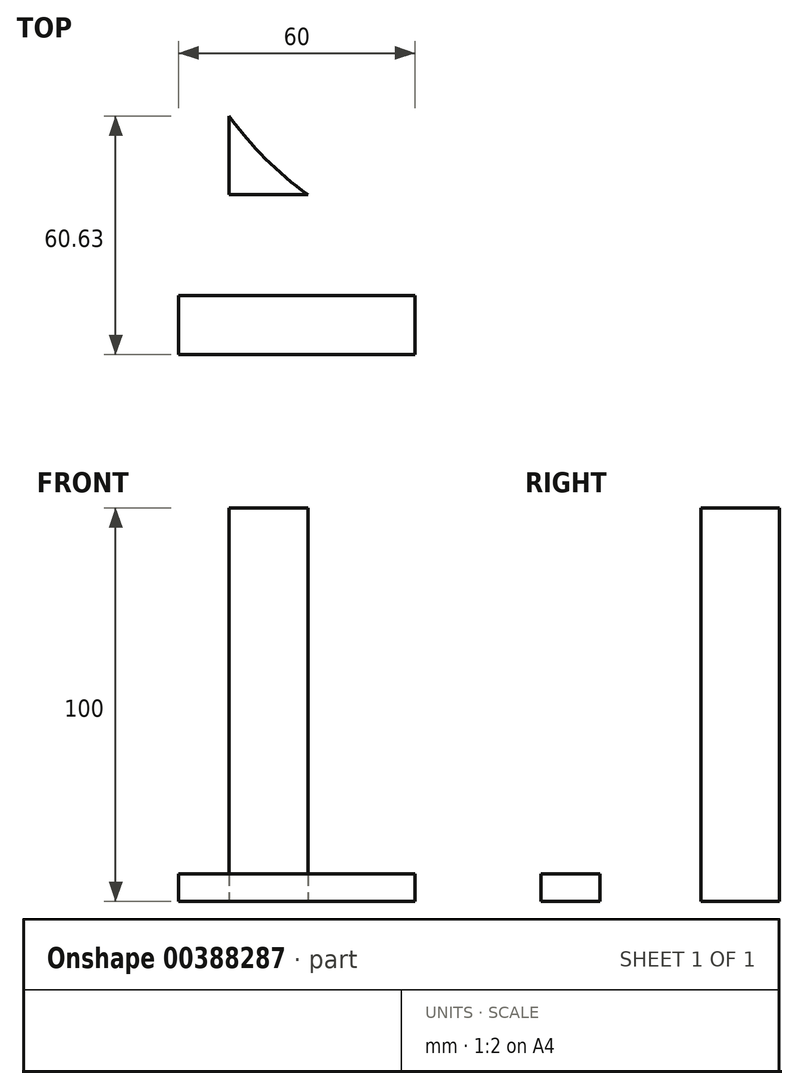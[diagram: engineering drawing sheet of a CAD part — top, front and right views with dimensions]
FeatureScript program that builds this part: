
annotation { "Feature Type Name" : "Feature", "Feature Type Description" : "" }
export const myFeature = defineFeature(function(context is Context, id is Id, definition is map)
    precondition{}
    {
        {
            var Q0;
            Q0=qCreatedBy(makeId("Top.planeOp"),FACE);
            var sketch = newSketch(context, id + "F0", { "sketchPlane" : qUnion([Q0])});
            skLineSegment(sketch, "E0.bottom", {"start": v(-10, -10) * mm, "end": v(10, -10) * mm});
            skLineSegment(sketch, "E0.left", {"start": v(-10, -10) * mm, "end": v(-10, 10) * mm});
            skArc(sketch, "E1", {"start": v(-10, 10) * mm, "mid": v(-0.8, -0.8) * mm, "end": v(10, -10) * mm});
            skSolve(sketch);
        }
        {
            var Q0;
            Q0 = qSketchRegion(id + "F0", true);
            extrude(context, id + "F1", {"entities" : qUnion([Q0]), "depth" : 100 * mm});
        }
        {
            var Q0;
            Q0=qCreatedBy(makeId("Top.planeOp"),FACE);
            var sketch = newSketch(context, id + "F2", { "sketchPlane" : qUnion([Q0])});
            skLineSegment(sketch, "E2.bottom", {"start": v(-22.8, -35.63) * mm, "end": v(37.2, -35.63) * mm});
            skLineSegment(sketch, "E2.top", {"start": v(-22.8, -50.63) * mm, "end": v(37.2, -50.63) * mm});
            skLineSegment(sketch, "E2.left", {"start": v(-22.8, -35.63) * mm, "end": v(-22.8, -50.63) * mm});
            skLineSegment(sketch, "E2.right", {"start": v(37.2, -35.63) * mm, "end": v(37.2, -50.63) * mm});
            skSolve(sketch);
        }
        {
            var Q0;
            Q0 = qSketchRegion(id + "F2", true);
            extrude(context, id + "F3", {"entities" : qUnion([Q0]), "depth" : 7 * mm, "offsetDistance" : 25 * mm});
        }
    });
